# Revit family: VL2MF-KARO-S-xWSxS0250
name_source: partatom
category: Leuchten
units: mm (PartAtom-declared; Revit-internal decimal feet)

## family parameters
Basisbauteil = Fläche
Beim Laden mit Abzugskörper schneiden = Nein
Bemaßung runder Anschluss = Durchmesser verwenden
Gemeinsam genutzt = Nein
Lichtquelle = Ja
OmniClass-Nummer = 23.80.70.11
OmniClass-Titel = Luminaries for Internal Lighting
Raumberechnungspunkt = Nein
Teiletyp = Normal

## types (4) — shared parameters
Baugruppenkennzeichen = D5020200
Datei für fotometrisches Netz = VL2MF-KARO-x_S.IES
Emissionsform beim Rendern sichtbar = Nein
Farbfilter = 16777215
Farbtemperaturverschiebung bei Dämpfen der Lampe = <Keine Auswahl>
Hersteller = RIDI Leuchten GmbH
Lampe = LED
Neigungswinkel = 90.00°
Scheinlast = 27 VA
URL = www.ridi.de
Von Breite des Rechtecks ausssenden = 93 mm  [stored 0.305118 ft]
Von Länge des Rechtecks aussenden = 93 mm  [stored 0.305118 ft]
brand = RIDI
conformity mark = CE
electrical safety class = 1
height = 188 mm  [stored 0.616798 ft]
ingress protection (IP) code = IP20
length = 500 mm  [stored 1.64042 ft]
nominal frequency = 50-60Hz
nominal voltage = 230
rated input power = 27
voltage type (AC, DC, UC) = AC
weight = 1.13 kg
width = 100 mm  [stored 0.328084 ft]
zero-valued in all types: Vorgabe-Ansicht

## per-type parameters (varying)
| type | Modell |
| VL2MF-KARO-S-5NDWS840S0250 | 0321884//696 |
| VL2MF-KARO-S-5NDWS830S0250 | 0321891//696 |
| VL2MF-KARO-S-7DAWS840S0250 | 0331884//696 |
| VL2MF-KARO-S-7DAWS830S0250 | 0331891//696 |

note: column(s) folded — value = type name in every type: product name

note: [stored X ft] marks values corroborated as IEEE doubles in the binary element streams (Revit-internal decimal feet)
